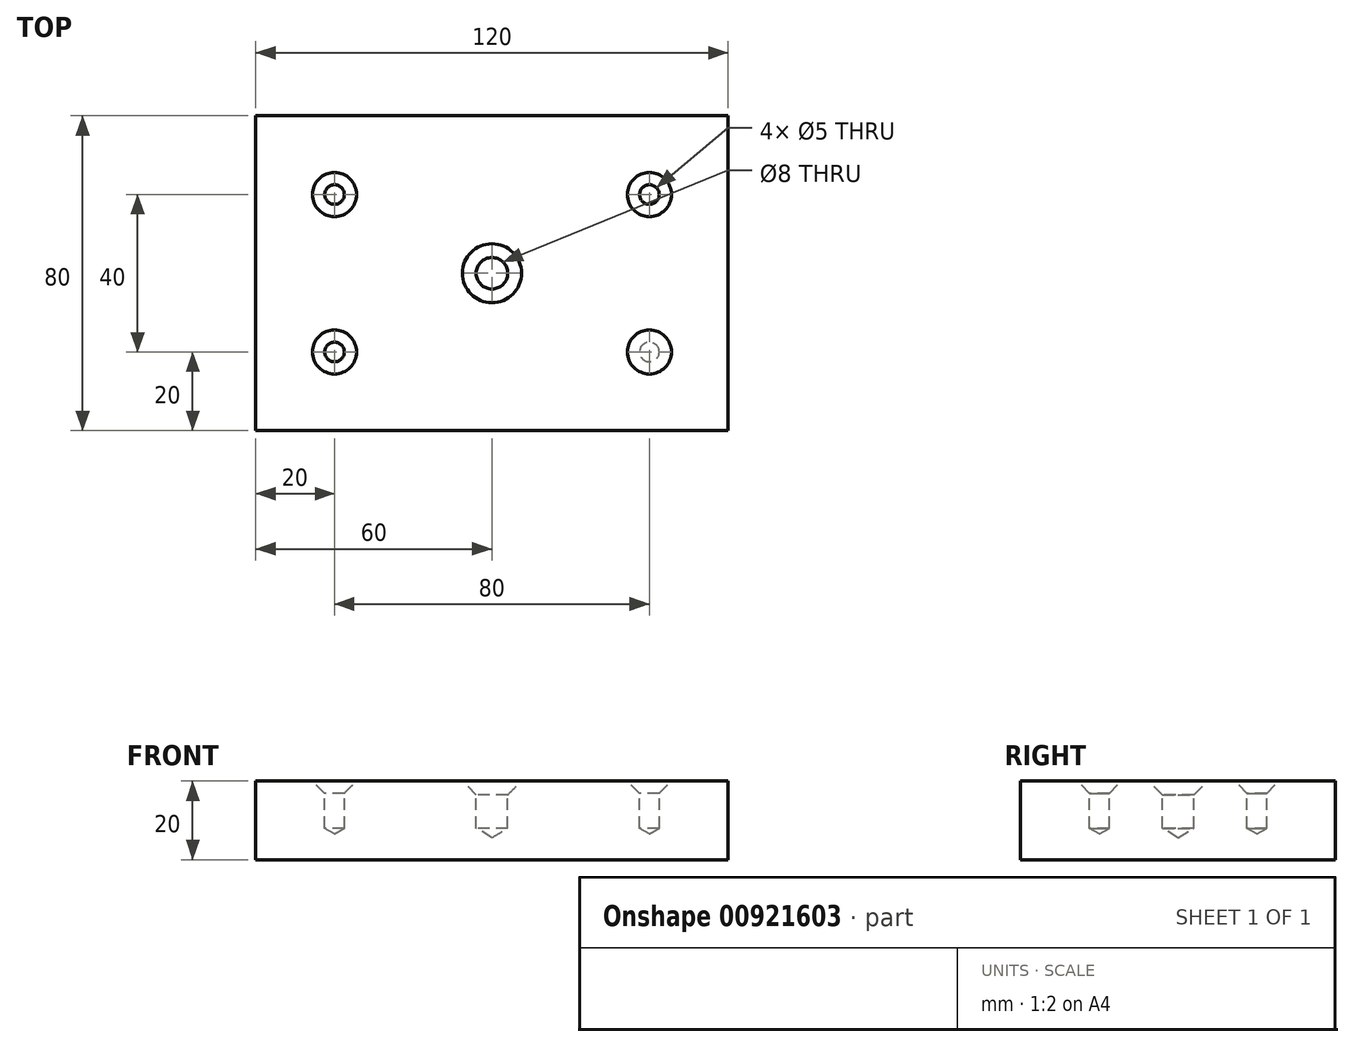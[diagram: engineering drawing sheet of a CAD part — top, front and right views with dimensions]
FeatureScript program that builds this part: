
annotation { "Feature Type Name" : "Feature", "Feature Type Description" : "" }
export const myFeature = defineFeature(function(context is Context, id is Id, definition is map)
    precondition{}
    {
        {
            var Q0;
            Q0=qCreatedBy(makeId("Top.planeOp"),FACE);
            var sketch = newSketch(context, id + "F0", { "sketchPlane" : qUnion([Q0])});
            skLineSegment(sketch, "E0.bottom", {"start": v(60, 40) * mm, "end": v(-60, 40) * mm});
            skLineSegment(sketch, "E0.top", {"start": v(60, -40) * mm, "end": v(-60, -40) * mm});
            skLineSegment(sketch, "E0.left", {"start": v(60, 40) * mm, "end": v(60, -40) * mm});
            skLineSegment(sketch, "E0.right", {"start": v(-60, 40) * mm, "end": v(-60, -40) * mm});
            skPoint(sketch, "E0.middle", {"position": v(0, 0) * mm});
            skSolve(sketch);
        }
        {
            var Q0;
            Q0 = qSketchRegion(id + "F0", true);
            extrude(context, id + "F1", {"entities" : qUnion([Q0]), "depth" : 20 * mm, "offsetDistance" : 25 * mm});
        }
        {
            var Q0;
            Q0=makeQuery(id+"F1.opExtrude","CAP_FACE",FACE,{"disambiguationData":[OSD([sQuery(id+"F0.wireOp",EDGE,"E0.bottom"),sQuery(id+"F0.wireOp",EDGE,"E0.top"),sQuery(id+"F0.wireOp",EDGE,"E0.left"),sQuery(id+"F0.wireOp",EDGE,"E0.right")])],"isStart":false});
            var sketch = newSketch(context, id + "F2", { "sketchPlane" : qUnion([Q0])});
            skPoint(sketch, "E1", {"position": v(-40, -20) * mm});
            skPoint(sketch, "E2.MirrorP", {"position": v(40, -20) * mm});
            skPoint(sketch, "E3.MirrorP", {"position": v(-40, 20) * mm});
            skPoint(sketch, "E4.MirrorP", {"position": v(40, 20) * mm});
            skSolve(sketch);
        }
        {
            var Q0;
            Q0=sQuery(id+"F2.wireOp",VERTEX,"E1");
            var Q1;
            Q1=sQuery(id+"F2.wireOp",VERTEX,"E2.MirrorP");
            var Q2;
            Q2=sQuery(id+"F2.wireOp",VERTEX,"E4.MirrorP");
            var Q3;
            Q3=sQuery(id+"F2.wireOp",VERTEX,"E3.MirrorP");
            var Q4;
            Q4=makeQuery(id+"F1.opExtrude","SWEPT_BODY",BODY,{"disambiguationData":[OSD([sQuery(id+"F0.wireOp",EDGE,"E0.bottom"),sQuery(id+"F0.wireOp",EDGE,"E0.top"),sQuery(id+"F0.wireOp",EDGE,"E0.left"),sQuery(id+"F0.wireOp",EDGE,"E0.right")])]});
            hole(context, id + "F3", {"style" : HoleStyle.C_SINK, "endStyle" : HoleEndStyle.BLIND, "holeDiameter" : 5 * mm, "cSinkDiameter" : 11.2 * mm, "cSinkAngle" : 90 * degree, "majorDiameter" : 5 * mm, "holeDepth" : 12 * mm, "isTappedThrough" : true, "tappedDepth" : 12 * mm, "tapClearance" : 3, "startFromSketch" : true, "locations" : qUnion([Q0, Q1, Q2, Q3]), "scope" : qUnion([Q4])});
        }
        {
            var Q0;
            Q0=makeQuery(id+"F1.opExtrude","CAP_FACE",FACE,{"disambiguationData":[OSD([sQuery(id+"F0.wireOp",EDGE,"E0.bottom"),sQuery(id+"F0.wireOp",EDGE,"E0.top"),sQuery(id+"F0.wireOp",EDGE,"E0.left"),sQuery(id+"F0.wireOp",EDGE,"E0.right")])],"isStart":false});
            var sketch = newSketch(context, id + "F4", { "sketchPlane" : qUnion([Q0])});
            skCircle(sketch, "E5.0", {"center": v(40, -20) * mm, "radius": 5.6 * mm});
            skSolve(sketch);
        }
        {
            var Q0;
            Q0 = qSketchRegion(id + "F4", true);
            extrude(context, id + "F5", {"entities" : qUnion([Q0]), "oppositeDirection" : true, "depth" : 20 * mm, "offsetDistance" : 25 * mm});
        }
        {
            var Q0;
            Q0=makeQuery(id+"F1.opExtrude","SWEPT_BODY",BODY,{"disambiguationData":[OSD([sQuery(id+"F0.wireOp",EDGE,"E0.bottom"),sQuery(id+"F0.wireOp",EDGE,"E0.top"),sQuery(id+"F0.wireOp",EDGE,"E0.left"),sQuery(id+"F0.wireOp",EDGE,"E0.right")])]});
            var Q1;
            Q1=makeQuery(id+"F5.opExtrude","SWEPT_BODY",BODY,{"disambiguationData":[OSD([sQuery(id+"F4.wireOp",EDGE,"E5.0")])]});
            booleanBodies(context, id + "F6", {"operationType" : BooleanOperationType.SUBTRACTION, "tools" : qUnion([Q0]), "targets" : qUnion([Q1]), "keepTools" : true});
        }
        {
            var Q0;
            Q0=makeQuery(id+"F1.opExtrude","CAP_FACE",FACE,{"disambiguationData":[OSD([sQuery(id+"F0.wireOp",EDGE,"E0.bottom"),sQuery(id+"F0.wireOp",EDGE,"E0.top"),sQuery(id+"F0.wireOp",EDGE,"E0.left"),sQuery(id+"F0.wireOp",EDGE,"E0.right")])],"isStart":false});
            var sketch = newSketch(context, id + "F7", { "sketchPlane" : qUnion([Q0])});
            skPoint(sketch, "E6", {"position": v(0, 0) * mm});
            skSolve(sketch);
        }
        {
            var Q0;
            Q0=sQuery(id+"F7.wireOp",VERTEX,"E6");
            var Q1;
            Q1=makeQuery(id+"F1.opExtrude","SWEPT_BODY",BODY,{"disambiguationData":[OSD([sQuery(id+"F0.wireOp",EDGE,"E0.bottom"),sQuery(id+"F0.wireOp",EDGE,"E0.top"),sQuery(id+"F0.wireOp",EDGE,"E0.left"),sQuery(id+"F0.wireOp",EDGE,"E0.right")])]});
            hole(context, id + "F8", {"style" : HoleStyle.C_SINK, "endStyle" : HoleEndStyle.BLIND, "holeDiameter" : 8 * mm, "cSinkDiameter" : 15 * mm, "cSinkAngle" : 90 * degree, "majorDiameter" : 5 * mm, "holeDepth" : 12 * mm, "isTappedThrough" : true, "tappedDepth" : 12 * mm, "tapClearance" : 3, "startFromSketch" : true, "locations" : qUnion([Q0]), "scope" : qUnion([Q1])});
        }
    });
